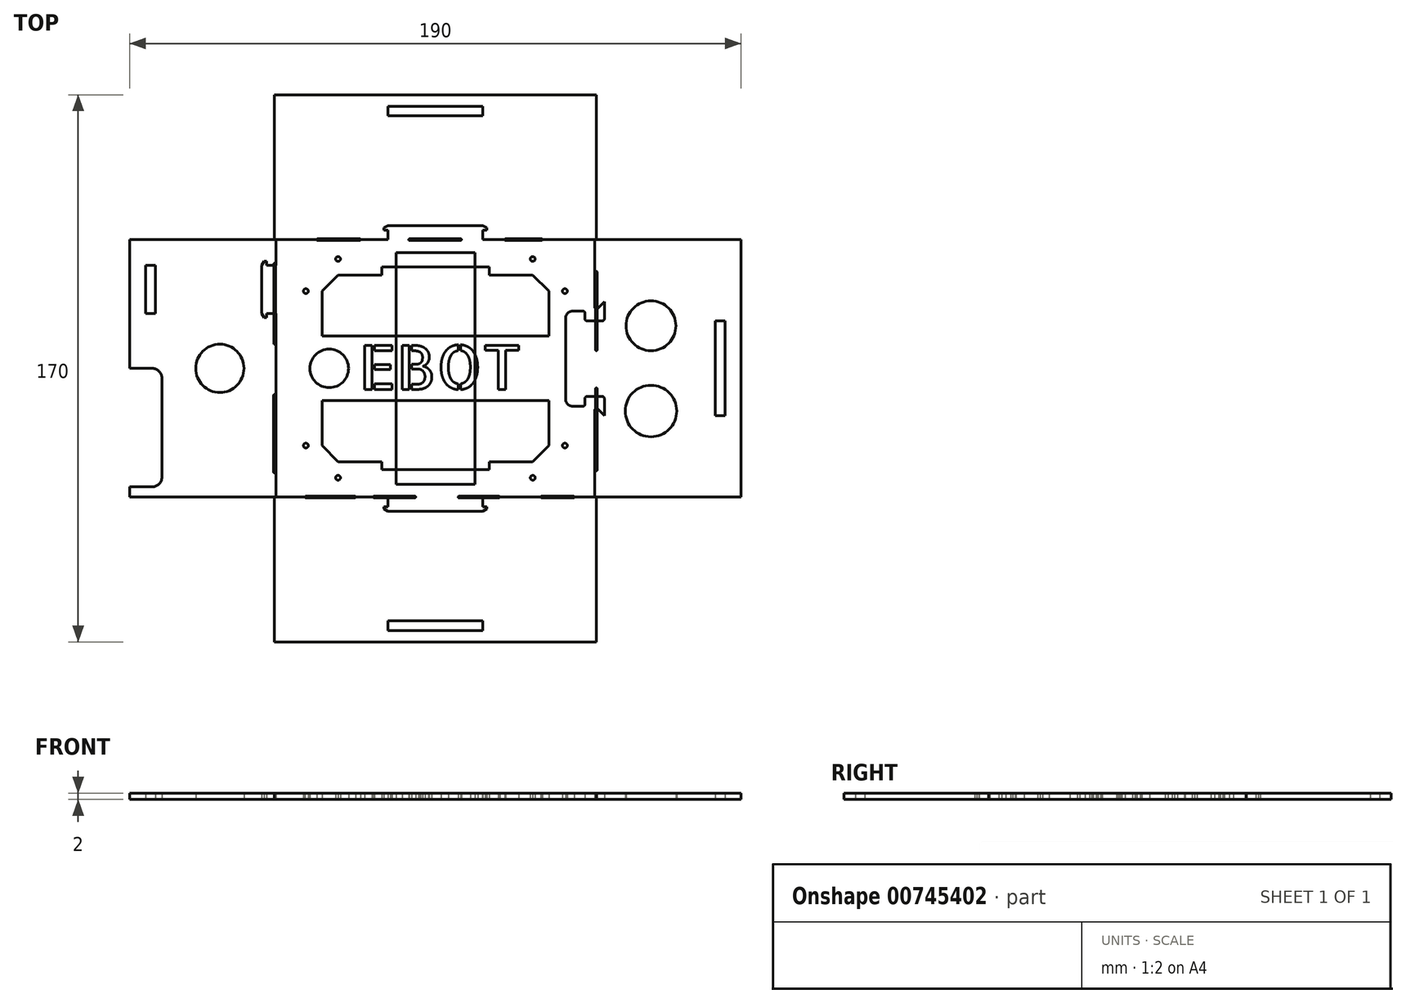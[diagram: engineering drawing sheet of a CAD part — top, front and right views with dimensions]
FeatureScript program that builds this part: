
annotation { "Feature Type Name" : "Feature", "Feature Type Description" : "" }
export const myFeature = defineFeature(function(context is Context, id is Id, definition is map)
    precondition{}
    {
        {
            var Q0;
            Q0=qCreatedBy(makeId("Top.planeOp"),FACE);
            var sketch = newSketch(context, id + "F0", { "sketchPlane" : qUnion([Q0])});
            skLineSegment(sketch, "E0.bottom", {"start": v(49.5, -40) * mm, "end": v(14.75, -40) * mm});
            skLineSegment(sketch, "E0.top", {"start": v(49.5, 40) * mm, "end": v(14.75, 40) * mm});
            skLineSegment(sketch, "E0.left", {"start": v(49.5, -40) * mm, "end": v(49.5, -13.1) * mm});
            skLineSegment(sketch, "E0.right", {"start": v(-49.5, -40) * mm, "end": v(-49.5, 17) * mm});
            skPoint(sketch, "E0.middle", {"position": v(0, 0) * mm});
            skLineSegment(sketch, "E1", {"start": v(14.75, 43) * mm, "end": v(14.75, 40) * mm});
            skLineSegment(sketch, "E2", {"start": v(-14.75, 43) * mm, "end": v(-14.75, 40) * mm});
            skLineSegment(sketch, "E3.trimOffspring", {"start": v(-14.75, 40) * mm, "end": v(-49.5, 40) * mm});
            skPoint(sketch, "E4.start.orphan", {"position": v(0, 40) * mm});
            skLineSegment(sketch, "E5", {"start": v(14.75, -43) * mm, "end": v(14.75, -40) * mm});
            skLineSegment(sketch, "E6", {"start": v(-14.75, -43) * mm, "end": v(-14.75, -40) * mm});
            skPoint(sketch, "E7.start.orphan", {"position": v(0, -40) * mm});
            skLineSegment(sketch, "E8.trimOffspring", {"start": v(-14.75, -40) * mm, "end": v(-49.5, -40) * mm});
            skLineSegment(sketch, "E9", {"start": v(-30.25, -29) * mm, "end": v(-35.25, -24) * mm});
            skLineSegment(sketch, "E10", {"start": v(30.25, -29) * mm, "end": v(35.25, -24) * mm});
            skLineSegment(sketch, "E11", {"start": v(-30.25, 29) * mm, "end": v(-35.25, 24) * mm});
            skLineSegment(sketch, "E12", {"start": v(30.25, 29) * mm, "end": v(35.25, 24) * mm});
            skLineSegment(sketch, "E13.bottom", {"start": v(35.25, -10.02) * mm, "end": v(-35.25, -10.02) * mm});
            skLineSegment(sketch, "E13.top", {"start": v(35.25, 10.02) * mm, "end": v(-35.25, 10.02) * mm});
            skLineSegment(sketch, "E14", {"start": v(-35.25, 24) * mm, "end": v(-35.25, 10.02) * mm});
            skLineSegment(sketch, "E15", {"start": v(35.25, 10.02) * mm, "end": v(35.25, 24) * mm});
            skLineSegment(sketch, "E16", {"start": v(30.25, 29) * mm, "end": v(16.69, 29) * mm});
            skLineSegment(sketch, "E17", {"start": v(35.25, -10.02) * mm, "end": v(35.25, -24) * mm});
            skLineSegment(sketch, "E18", {"start": v(30.25, -29) * mm, "end": v(16.69, -29) * mm});
            skLineSegment(sketch, "E19", {"start": v(-35.25, -24) * mm, "end": v(-35.25, -10.02) * mm});
            skLineSegment(sketch, "E20", {"start": v(35.25, 24) * mm, "end": v(40.25, 24) * mm});
            skLineSegment(sketch, "E21", {"start": v(30.25, 29) * mm, "end": v(30.25, 34) * mm});
            skLineSegment(sketch, "E22", {"start": v(-35.25, 24) * mm, "end": v(-40.25, 24) * mm});
            skLineSegment(sketch, "E23", {"start": v(-30.25, 29) * mm, "end": v(-30.25, 34) * mm});
            skLineSegment(sketch, "E24", {"start": v(-35.25, -24) * mm, "end": v(-40.25, -24) * mm});
            skLineSegment(sketch, "E25", {"start": v(-30.25, -29) * mm, "end": v(-30.25, -34) * mm});
            skLineSegment(sketch, "E26", {"start": v(35.25, -24) * mm, "end": v(40.25, -24) * mm});
            skLineSegment(sketch, "E27", {"start": v(30.25, -29) * mm, "end": v(30.25, -34) * mm});
            skLineSegment(sketch, "E28.top", {"start": v(16.69, 31.5) * mm, "end": v(-16.69, 31.5) * mm});
            skLineSegment(sketch, "E28.left", {"start": v(16.69, 29) * mm, "end": v(16.69, 31.5) * mm});
            skLineSegment(sketch, "E28.right", {"start": v(-16.69, 29) * mm, "end": v(-16.69, 31.5) * mm});
            skPoint(sketch, "E28.middle", {"position": v(0, 29) * mm});
            skLineSegment(sketch, "E29.top", {"start": v(16.69, -31.5) * mm, "end": v(-16.69, -31.5) * mm});
            skLineSegment(sketch, "E29.left", {"start": v(16.69, -29) * mm, "end": v(16.69, -31.5) * mm});
            skLineSegment(sketch, "E29.right", {"start": v(-16.69, -29) * mm, "end": v(-16.69, -31.5) * mm});
            skPoint(sketch, "E29.middle", {"position": v(0, -29) * mm});
            skLineSegment(sketch, "E30.trimOffspring", {"start": v(-16.69, 29) * mm, "end": v(-30.25, 29) * mm});
            skLineSegment(sketch, "E31.trimOffspring", {"start": v(-16.69, -29) * mm, "end": v(-30.25, -29) * mm});
            skLineSegment(sketch, "E32.bottom", {"start": v(45.49, 17.76) * mm, "end": v(42.49, 17.76) * mm});
            skLineSegment(sketch, "E32.top", {"start": v(45.49, -11.74) * mm, "end": v(42.49, -11.74) * mm});
            skLineSegment(sketch, "E32.right", {"start": v(40.49, 15.76) * mm, "end": v(40.49, -9.74) * mm});
            skPoint(sketch, "E33.visualSharp", {"position": v(40.49, 17.76) * mm});
            skArc(sketch, "E33.filletArc", {"start": v(42.49, 17.76) * mm, "mid": v(41.08, 17.17) * mm, "end": v(40.49, 15.76) * mm});
            skPoint(sketch, "E34.visualSharp", {"position": v(40.49, -11.74) * mm});
            skArc(sketch, "E34.filletArc", {"start": v(40.49, -9.74) * mm, "mid": v(41.08, -11.15) * mm, "end": v(42.49, -11.74) * mm});
            skLineSegment(sketch, "E35", {"start": v(45.49, 17.76) * mm, "end": v(45.93, 17.76) * mm});
            skLineSegment(sketch, "E36", {"start": v(45.93, -11.74) * mm, "end": v(45.49, -11.74) * mm});
            skCircle(sketch, "E37", {"center": v(30.25, 34) * mm, "radius": 0.75 * mm});
            skCircle(sketch, "E38", {"center": v(40.25, 24) * mm, "radius": 0.75 * mm});
            skCircle(sketch, "E39", {"center": v(40.25, -24) * mm, "radius": 0.75 * mm});
            skCircle(sketch, "E40", {"center": v(30.25, -34) * mm, "radius": 0.75 * mm});
            skCircle(sketch, "E41", {"center": v(-30.25, -34) * mm, "radius": 0.75 * mm});
            skCircle(sketch, "E42", {"center": v(-40.25, -24) * mm, "radius": 0.75 * mm});
            skCircle(sketch, "E43", {"center": v(-40.25, 24) * mm, "radius": 0.75 * mm});
            skCircle(sketch, "E44", {"center": v(-30.25, 34) * mm, "radius": 0.75 * mm});
            skLineSegment(sketch, "E45.bottom", {"start": v(14.75, 44.4) * mm, "end": v(-14.75, 44.4) * mm});
            skLineSegment(sketch, "E45.left", {"start": v(16, 43.7) * mm, "end": v(16, 43) * mm});
            skLineSegment(sketch, "E45.right", {"start": v(-16, 43.7) * mm, "end": v(-16, 43) * mm});
            skPoint(sketch, "E45.middle", {"position": v(0, 43) * mm});
            skLineSegment(sketch, "E46", {"start": v(-16, 43) * mm, "end": v(-14.75, 43) * mm});
            skPoint(sketch, "E47.orphan", {"position": v(16, 41.6) * mm});
            skPoint(sketch, "E48.orphan", {"position": v(-16, 41.6) * mm});
            skLineSegment(sketch, "E49.trimOffspring", {"start": v(14.75, 43) * mm, "end": v(16, 43) * mm});
            skLineSegment(sketch, "E50", {"start": v(16, 43.7) * mm, "end": v(14.75, 44.4) * mm});
            skLineSegment(sketch, "E51", {"start": v(-16, 43.7) * mm, "end": v(-14.75, 44.4) * mm});
            skPoint(sketch, "E52.orphan", {"position": v(-16, 44.4) * mm});
            skPoint(sketch, "E53.orphan", {"position": v(16, 44.4) * mm});
            skLineSegment(sketch, "E54.MirrorCS", {"start": v(16, -43.7) * mm, "end": v(16, -43) * mm});
            skLineSegment(sketch, "E55.MirrorCS", {"start": v(-16, -43.7) * mm, "end": v(-16, -43) * mm});
            skLineSegment(sketch, "E56.MirrorCS", {"start": v(-16, -43.7) * mm, "end": v(-14.75, -44.4) * mm});
            skLineSegment(sketch, "E57.MirrorCS", {"start": v(14.75, -43) * mm, "end": v(16, -43) * mm});
            skLineSegment(sketch, "E58.MirrorCS", {"start": v(16, -43.7) * mm, "end": v(14.75, -44.4) * mm});
            skLineSegment(sketch, "E59.MirrorCS", {"start": v(-16, -43) * mm, "end": v(-14.75, -43) * mm});
            skLineSegment(sketch, "E60.MirrorCS", {"start": v(14.75, -44.4) * mm, "end": v(-14.75, -44.4) * mm});
            skPoint(sketch, "E61.MirrorP", {"position": v(0, -43) * mm});
            skPoint(sketch, "E62.MirrorP", {"position": v(16, -41.6) * mm});
            skPoint(sketch, "E63.MirrorP", {"position": v(16, -44.4) * mm});
            skPoint(sketch, "E64.MirrorP", {"position": v(-16, -41.6) * mm});
            skPoint(sketch, "E65.MirrorP", {"position": v(-16, -44.4) * mm});
            skLineSegment(sketch, "E66", {"start": v(-49.5, 40) * mm, "end": v(-49.5, 32) * mm, "construction": true});
            skLineSegment(sketch, "E67", {"start": v(-49.5, 32) * mm, "end": v(-52.5, 32) * mm});
            skLineSegment(sketch, "E68", {"start": v(-52.5, 17) * mm, "end": v(-49.5, 17) * mm});
            skLineSegment(sketch, "E69.bottom", {"start": v(-52.5, 15.75) * mm, "end": v(-53.25, 15.75) * mm});
            skLineSegment(sketch, "E69.top", {"start": v(-52.5, 33.25) * mm, "end": v(-53.25, 33.25) * mm});
            skLineSegment(sketch, "E69.right", {"start": v(-54, 17) * mm, "end": v(-54, 32) * mm});
            skPoint(sketch, "E69.cornerSnap0", {"position": v(-51, 17) * mm});
            skLineSegment(sketch, "E70", {"start": v(-52.5, 33.25) * mm, "end": v(-52.5, 32) * mm});
            skPoint(sketch, "E71.orphan", {"position": v(-51, 15.75) * mm});
            skPoint(sketch, "E72.orphan", {"position": v(-51, 33.25) * mm});
            skLineSegment(sketch, "E73", {"start": v(-53.25, 33.25) * mm, "end": v(-54, 32) * mm});
            skLineSegment(sketch, "E74", {"start": v(-53.25, 15.75) * mm, "end": v(-54, 17) * mm});
            skPoint(sketch, "E75.orphan", {"position": v(-54, 15.75) * mm});
            skPoint(sketch, "E76.orphan", {"position": v(-54, 33.25) * mm});
            skLineSegment(sketch, "E77.trimOffspring", {"start": v(-52.5, 17) * mm, "end": v(-52.5, 15.75) * mm});
            skLineSegment(sketch, "E78.trimOffspring", {"start": v(-49.5, 32) * mm, "end": v(-49.5, 40) * mm});
            skLineSegment(sketch, "E79", {"start": v(49.5, 40) * mm, "end": v(49.5, 19.13) * mm});
            skLineSegment(sketch, "E80.bottom", {"start": v(51.93, 14.76) * mm, "end": v(47.07, 14.76) * mm});
            skLineSegment(sketch, "E80.left", {"start": v(52.5, 15.33) * mm, "end": v(52.5, 20.76) * mm});
            skLineSegment(sketch, "E80.right", {"start": v(46.5, 15.33) * mm, "end": v(46.5, 17.2) * mm});
            skPoint(sketch, "E80.middle", {"position": v(49.5, 17.76) * mm});
            skLineSegment(sketch, "E81.top", {"start": v(51.93, -8.74) * mm, "end": v(47.07, -8.74) * mm});
            skLineSegment(sketch, "E81.left", {"start": v(52.5, -14.74) * mm, "end": v(52.5, -9.3) * mm});
            skPoint(sketch, "E81.middle", {"position": v(49.5, -11.74) * mm});
            skLineSegment(sketch, "E82", {"start": v(50.47, 18.73) * mm, "end": v(52.5, 20.76) * mm});
            skLineSegment(sketch, "E83", {"start": v(50.47, -12.7) * mm, "end": v(52.5, -14.74) * mm});
            skLineSegment(sketch, "E84", {"start": v(46.5, -9.3) * mm, "end": v(46.5, -11.17) * mm});
            skArc(sketch, "E85.filletArc", {"start": v(45.93, -11.74) * mm, "mid": v(46.33, -11.57) * mm, "end": v(46.5, -11.17) * mm});
            skPoint(sketch, "E86.visualSharp", {"position": v(46.5, -8.74) * mm});
            skArc(sketch, "E86.filletArc", {"start": v(47.07, -8.74) * mm, "mid": v(46.67, -8.9) * mm, "end": v(46.5, -9.3) * mm});
            skPoint(sketch, "E87.visualSharp", {"position": v(52.5, -8.74) * mm});
            skArc(sketch, "E87.filletArc", {"start": v(52.5, -9.3) * mm, "mid": v(52.33, -8.9) * mm, "end": v(51.93, -8.74) * mm});
            skArc(sketch, "E88.filletArc", {"start": v(50.47, -12.7) * mm, "mid": v(49.85, -12.58) * mm, "end": v(49.5, -13.1) * mm});
            skPoint(sketch, "E80.top.end.orphan", {"position": v(46.5, 20.76) * mm});
            skPoint(sketch, "E89.visualSharp", {"position": v(46.5, 17.76) * mm});
            skArc(sketch, "E89.filletArc", {"start": v(46.5, 17.2) * mm, "mid": v(46.33, 17.6) * mm, "end": v(45.93, 17.76) * mm});
            skPoint(sketch, "E90.visualSharp", {"position": v(46.5, 14.76) * mm});
            skArc(sketch, "E90.filletArc", {"start": v(46.5, 15.33) * mm, "mid": v(46.67, 14.93) * mm, "end": v(47.07, 14.76) * mm});
            skPoint(sketch, "E91.visualSharp", {"position": v(52.5, 14.76) * mm});
            skArc(sketch, "E91.filletArc", {"start": v(51.93, 14.76) * mm, "mid": v(52.33, 14.93) * mm, "end": v(52.5, 15.33) * mm});
            skArc(sketch, "E92.filletArc", {"start": v(49.5, 19.13) * mm, "mid": v(49.85, 18.6) * mm, "end": v(50.47, 18.73) * mm});
            skText(sketch, "E93", { "text": "EBOT", "fontName": "AllertaStencil-Regular.ttf"});
            skLineSegment(sketch, "E94", {"start": v(-35.25, 24) * mm, "end": v(-35.25, 29) * mm, "construction": true});
            skLineSegment(sketch, "E95", {"start": v(-35.25, 29) * mm, "end": v(-30.25, 29) * mm, "construction": true});
            skLineSegment(sketch, "E96", {"start": v(30.25, 29) * mm, "end": v(35.25, 29) * mm, "construction": true});
            skLineSegment(sketch, "E97", {"start": v(35.25, 29) * mm, "end": v(35.25, 24) * mm, "construction": true});
            skLineSegment(sketch, "E98", {"start": v(35.25, -24) * mm, "end": v(35.25, -29) * mm, "construction": true});
            skLineSegment(sketch, "E99", {"start": v(35.25, -29) * mm, "end": v(30.25, -29) * mm, "construction": true});
            skLineSegment(sketch, "E100", {"start": v(-35.25, -24) * mm, "end": v(-35.25, -29) * mm, "construction": true});
            skLineSegment(sketch, "E101", {"start": v(-35.25, -29) * mm, "end": v(-30.25, -29) * mm, "construction": true});
            const initialGuessF0  = {"E93": [-0.02376, -0.00652, 1, 0, 0.01367]};
            skSetInitialGuess(sketch, initialGuessF0);
            skSolve(sketch);
        }
        {
            var Q0;
            Q0=qCreatedBy(makeId("Top.planeOp"),FACE);
            var sketch = newSketch(context, id + "F1", { "sketchPlane" : qUnion([Q0])});
            skLineSegment(sketch, "E102.bottom", {"start": v(50, -40) * mm, "end": v(50, -85) * mm});
            skLineSegment(sketch, "E103.top", {"start": v(95, -40) * mm, "end": v(95, 40) * mm});
            skLineSegment(sketch, "E103.left", {"start": v(50, -40) * mm, "end": v(72.5, -40) * mm});
            skLineSegment(sketch, "E103.right", {"start": v(50, 40) * mm, "end": v(72.5, 40) * mm});
            skLineSegment(sketch, "E104.bottom", {"start": v(50, 40) * mm, "end": v(50, 85) * mm});
            skLineSegment(sketch, "E104.top", {"start": v(-50, 40) * mm, "end": v(-50, 85) * mm});
            skLineSegment(sketch, "E104.right", {"start": v(50, 85) * mm, "end": v(-50, 85) * mm});
            skLineSegment(sketch, "E105.top", {"start": v(-95, 40) * mm, "end": v(-95, 0) * mm});
            skLineSegment(sketch, "E105.left", {"start": v(-49.99, 40) * mm, "end": v(-72.5, 40) * mm});
            skLineSegment(sketch, "E105.right", {"start": v(-50, -40) * mm, "end": v(-72.5, -40) * mm});
            skLineSegment(sketch, "E106", {"start": v(-50, 0) * mm, "end": v(-67, 0) * mm, "construction": true});
            skPoint(sketch, "E107.startSnap0", {"position": v(0, -40) * mm});
            skLineSegment(sketch, "E108", {"start": v(-50, -85) * mm, "end": v(50, -85) * mm});
            skLineSegment(sketch, "E109", {"start": v(-50, -85) * mm, "end": v(-50, -40) * mm});
            skLineSegment(sketch, "E110", {"start": v(0, -85) * mm, "end": v(0, -80) * mm, "construction": true});
            skLineSegment(sketch, "E111.bottom", {"start": v(14.75, -81.5) * mm, "end": v(-14.75, -81.5) * mm});
            skLineSegment(sketch, "E111.top", {"start": v(14.75, -78.5) * mm, "end": v(-14.75, -78.5) * mm});
            skLineSegment(sketch, "E111.left", {"start": v(14.75, -81.5) * mm, "end": v(14.75, -78.5) * mm});
            skLineSegment(sketch, "E111.right", {"start": v(-14.75, -81.5) * mm, "end": v(-14.75, -78.5) * mm});
            skPoint(sketch, "E111.middle", {"position": v(0, -80) * mm});
            skLineSegment(sketch, "E112", {"start": v(0, 85) * mm, "end": v(0, 80) * mm, "construction": true});
            skLineSegment(sketch, "E113.bottom", {"start": v(14.75, 78.5) * mm, "end": v(-14.75, 78.5) * mm});
            skLineSegment(sketch, "E113.top", {"start": v(14.75, 81.5) * mm, "end": v(-14.75, 81.5) * mm});
            skLineSegment(sketch, "E113.left", {"start": v(14.75, 78.5) * mm, "end": v(14.75, 81.5) * mm});
            skLineSegment(sketch, "E113.right", {"start": v(-14.75, 78.5) * mm, "end": v(-14.75, 81.5) * mm});
            skPoint(sketch, "E113.middle", {"position": v(0, 80) * mm});
            skLineSegment(sketch, "E114", {"start": v(-95, 0) * mm, "end": v(-85, 0) * mm, "construction": true});
            skLineSegment(sketch, "E115", {"start": v(-95, 0) * mm, "end": v(-88, 0) * mm});
            skLineSegment(sketch, "E116", {"start": v(-85, -33.83) * mm, "end": v(-85, -3) * mm});
            skPoint(sketch, "E117.visualSharp", {"position": v(-85, 0) * mm});
            skArc(sketch, "E117.filletArc", {"start": v(-85, -3) * mm, "mid": v(-85.88, -0.88) * mm, "end": v(-88, 0) * mm});
            skLineSegment(sketch, "E118", {"start": v(-88, -36.83) * mm, "end": v(-95, -36.83) * mm});
            skArc(sketch, "E119.filletArc", {"start": v(-88, -36.83) * mm, "mid": v(-85.88, -35.95) * mm, "end": v(-85, -33.83) * mm});
            skLineSegment(sketch, "E120.trimOffspring", {"start": v(-95, -36.83) * mm, "end": v(-95, -40) * mm});
            skCircle(sketch, "E121", {"center": v(-33, 0) * mm, "radius": 6 * mm});
            skCircle(sketch, "E122", {"center": v(-67, 0) * mm, "radius": 7.5 * mm});
            skLineSegment(sketch, "E123", {"start": v(50, 40) * mm, "end": v(33, 40) * mm, "construction": true});
            skLineSegment(sketch, "E124", {"start": v(50, 0) * mm, "end": v(67, 0) * mm, "construction": true});
            skLineSegment(sketch, "E125.trimOffspring", {"start": v(87.5, 40) * mm, "end": v(95, 40) * mm});
            skPoint(sketch, "E126.oppositeSnap0", {"position": v(72.5, -40) * mm});
            skLineSegment(sketch, "E127.trimOffspring", {"start": v(87.5, -40) * mm, "end": v(95, -40) * mm});
            skPoint(sketch, "E128.firstSnap0", {"position": v(-72.5, -40) * mm});
            skLineSegment(sketch, "E128.bottom", {"start": v(-72.5, -40) * mm, "end": v(-72.5, -40) * mm});
            skLineSegment(sketch, "E129.trimOffspring", {"start": v(-87.5, -40) * mm, "end": v(-95, -40) * mm});
            skLineSegment(sketch, "E130.trimOffspring", {"start": v(-87.5, 40) * mm, "end": v(-95, 40) * mm});
            skLineSegment(sketch, "E131", {"start": v(-87.5, 40) * mm, "end": v(-72.5, 40) * mm});
            skLineSegment(sketch, "E132", {"start": v(-72.5, -40) * mm, "end": v(-87.5, -40) * mm});
            skLineSegment(sketch, "E133", {"start": v(72.5, -40) * mm, "end": v(87.5, -40) * mm});
            skLineSegment(sketch, "E134", {"start": v(-49.99, 32.47) * mm, "end": v(-49.99, 7.79) * mm});
            skLineSegment(sketch, "E135", {"start": v(-50, -32.3) * mm, "end": v(-50, -8.35) * mm});
            skLineSegment(sketch, "E136", {"start": v(50, 29.94) * mm, "end": v(50, 5.74) * mm});
            skLineSegment(sketch, "E137", {"start": v(50, -31.59) * mm, "end": v(50, -6.35) * mm});
            skLineSegment(sketch, "E138", {"start": v(-40.23, -40) * mm, "end": v(-25.04, -40) * mm});
            skLineSegment(sketch, "E139", {"start": v(72.5, 40) * mm, "end": v(87.5, 40) * mm});
            skLineSegment(sketch, "E140.bottom", {"start": v(12.25, -36) * mm, "end": v(-12.25, -36) * mm});
            skLineSegment(sketch, "E140.top", {"start": v(12.25, 36) * mm, "end": v(-12.25, 36) * mm});
            skLineSegment(sketch, "E140.left", {"start": v(12.25, -36) * mm, "end": v(12.25, 36) * mm});
            skLineSegment(sketch, "E140.right", {"start": v(-12.25, -36) * mm, "end": v(-12.25, 36) * mm});
            skPoint(sketch, "E140.middle", {"position": v(0, 0) * mm});
            skLineSegment(sketch, "E141", {"start": v(67, 0) * mm, "end": v(67, 5.5) * mm, "construction": true});
            skLineSegment(sketch, "E142", {"start": v(67, 0) * mm, "end": v(67, -5.25) * mm, "construction": true});
            skLineSegment(sketch, "E143", {"start": v(67, -5.25) * mm, "end": v(67, -13.25) * mm, "construction": true});
            skCircle(sketch, "E144", {"center": v(67, -13.25) * mm, "radius": 8 * mm});
            skLineSegment(sketch, "E145", {"start": v(67, 5.25) * mm, "end": v(67, 13.25) * mm, "construction": true});
            skCircle(sketch, "E146", {"center": v(67, 13.25) * mm, "radius": 7.75 * mm});
            skLineSegment(sketch, "E147.3.0", {"start": v(87, -14.75) * mm, "end": v(90, -14.75) * mm});
            skLineSegment(sketch, "E147.3.1", {"start": v(87, -14.75) * mm, "end": v(87, 14.75) * mm});
            skLineSegment(sketch, "E147.3.2", {"start": v(90, -14.75) * mm, "end": v(90, 14.75) * mm});
            skLineSegment(sketch, "E147.3.3", {"start": v(87, 14.75) * mm, "end": v(90, 14.75) * mm});
            skPoint(sketch, "E147.center", {"position": v(4.25, -4.25) * mm});
            skLineSegment(sketch, "E148.bottom", {"start": v(-90, 32) * mm, "end": v(-87, 32) * mm});
            skLineSegment(sketch, "E148.top", {"start": v(-90, 17) * mm, "end": v(-87, 17) * mm});
            skLineSegment(sketch, "E148.left", {"start": v(-90, 32) * mm, "end": v(-90, 17) * mm});
            skLineSegment(sketch, "E148.right", {"start": v(-87, 32) * mm, "end": v(-87, 17) * mm});
            skLineSegment(sketch, "E149", {"start": v(-19.03, -39.98) * mm, "end": v(-6.4, -39.98) * mm});
            skLineSegment(sketch, "E150", {"start": v(-6.4, -39.98) * mm, "end": v(7.31, -39.98) * mm, "construction": true});
            skLineSegment(sketch, "E151", {"start": v(7.31, -39.98) * mm, "end": v(19.74, -40) * mm});
            skLineSegment(sketch, "E152", {"start": v(19.74, -40) * mm, "end": v(33, -40) * mm, "construction": true});
            skLineSegment(sketch, "E153", {"start": v(33, -40) * mm, "end": v(42.95, -40) * mm});
            skLineSegment(sketch, "E154", {"start": v(42.95, -40) * mm, "end": v(50, -40) * mm, "construction": true});
            skLineSegment(sketch, "E155", {"start": v(-49.99, 40) * mm, "end": v(-36.6, 40) * mm, "construction": true});
            skLineSegment(sketch, "E156", {"start": v(-36.6, 40) * mm, "end": v(-23.54, 40) * mm});
            skLineSegment(sketch, "E157", {"start": v(-23.54, 40) * mm, "end": v(-8.07, 40) * mm, "construction": true});
            skLineSegment(sketch, "E158", {"start": v(-8.07, 40) * mm, "end": v(7.85, 40) * mm});
            skLineSegment(sketch, "E159", {"start": v(7.85, 40) * mm, "end": v(21.78, 40) * mm, "construction": true});
            skLineSegment(sketch, "E160", {"start": v(21.78, 40) * mm, "end": v(33, 40) * mm});
            skArc(sketch, "E161.0.startCap", {"start": v(49.75, 29.94) * mm, "mid": v(50, 30.2) * mm, "end": v(50.25, 29.94) * mm});
            skArc(sketch, "E161.0.endCap", {"start": v(50.25, 5.74) * mm, "mid": v(50, 5.5) * mm, "end": v(49.75, 5.74) * mm});
            skLineSegment(sketch, "E161.0.left", {"start": v(50.25, 29.94) * mm, "end": v(50.25, 5.74) * mm});
            skLineSegment(sketch, "E161.0.right", {"start": v(49.75, 29.94) * mm, "end": v(49.75, 5.74) * mm});
            skArc(sketch, "E162.0.startCap", {"start": v(50.25, -31.59) * mm, "mid": v(50, -31.84) * mm, "end": v(49.75, -31.59) * mm});
            skArc(sketch, "E162.0.endCap", {"start": v(49.75, -6.35) * mm, "mid": v(50, -6.1) * mm, "end": v(50.25, -6.35) * mm});
            skLineSegment(sketch, "E162.0.left", {"start": v(49.75, -31.59) * mm, "end": v(49.75, -6.35) * mm});
            skLineSegment(sketch, "E162.0.right", {"start": v(50.25, -31.59) * mm, "end": v(50.25, -6.35) * mm});
            skArc(sketch, "E162.1.startCap", {"start": v(33, -40.25) * mm, "mid": v(32.74, -40) * mm, "end": v(33, -39.75) * mm});
            skArc(sketch, "E162.1.endCap", {"start": v(42.95, -39.75) * mm, "mid": v(43.2, -40) * mm, "end": v(42.95, -40.25) * mm});
            skLineSegment(sketch, "E162.1.left", {"start": v(33, -39.75) * mm, "end": v(42.95, -39.75) * mm});
            skLineSegment(sketch, "E162.1.right", {"start": v(33, -40.25) * mm, "end": v(42.95, -40.25) * mm});
            skArc(sketch, "E162.2.startCap", {"start": v(7.31, -40.23) * mm, "mid": v(7.06, -39.98) * mm, "end": v(7.31, -39.73) * mm});
            skArc(sketch, "E162.2.endCap", {"start": v(19.74, -39.75) * mm, "mid": v(20, -40) * mm, "end": v(19.74, -40.25) * mm});
            skLineSegment(sketch, "E162.2.left", {"start": v(7.31, -39.73) * mm, "end": v(19.74, -39.75) * mm});
            skLineSegment(sketch, "E162.2.right", {"start": v(7.31, -40.23) * mm, "end": v(19.74, -40.25) * mm});
            skArc(sketch, "E162.3.startCap", {"start": v(-19.03, -40.23) * mm, "mid": v(-19.28, -39.98) * mm, "end": v(-19.03, -39.73) * mm});
            skArc(sketch, "E162.3.endCap", {"start": v(-6.4, -39.73) * mm, "mid": v(-6.16, -39.98) * mm, "end": v(-6.4, -40.23) * mm});
            skLineSegment(sketch, "E162.3.left", {"start": v(-19.03, -39.73) * mm, "end": v(-6.4, -39.73) * mm});
            skLineSegment(sketch, "E162.3.right", {"start": v(-19.03, -40.23) * mm, "end": v(-6.4, -40.23) * mm});
            skArc(sketch, "E162.4.startCap", {"start": v(-40.23, -40.25) * mm, "mid": v(-40.48, -40) * mm, "end": v(-40.23, -39.75) * mm});
            skArc(sketch, "E162.4.endCap", {"start": v(-25.04, -39.75) * mm, "mid": v(-24.79, -40) * mm, "end": v(-25.04, -40.25) * mm});
            skLineSegment(sketch, "E162.4.left", {"start": v(-40.23, -39.75) * mm, "end": v(-25.04, -39.75) * mm});
            skLineSegment(sketch, "E162.4.right", {"start": v(-40.23, -40.25) * mm, "end": v(-25.04, -40.25) * mm});
            skArc(sketch, "E162.5.startCap", {"start": v(-49.75, -32.3) * mm, "mid": v(-50, -32.55) * mm, "end": v(-50.25, -32.3) * mm});
            skArc(sketch, "E162.5.endCap", {"start": v(-50.25, -8.35) * mm, "mid": v(-50, -8.1) * mm, "end": v(-49.75, -8.35) * mm});
            skLineSegment(sketch, "E162.5.left", {"start": v(-50.25, -32.3) * mm, "end": v(-50.25, -8.35) * mm});
            skLineSegment(sketch, "E162.5.right", {"start": v(-49.75, -32.3) * mm, "end": v(-49.75, -8.35) * mm});
            skArc(sketch, "E162.6.startCap", {"start": v(21.78, 39.75) * mm, "mid": v(21.53, 40) * mm, "end": v(21.78, 40.25) * mm});
            skArc(sketch, "E162.6.endCap", {"start": v(33, 40.25) * mm, "mid": v(33.25, 40) * mm, "end": v(33, 39.75) * mm});
            skLineSegment(sketch, "E162.6.left", {"start": v(21.78, 40.25) * mm, "end": v(33, 40.25) * mm});
            skLineSegment(sketch, "E162.6.right", {"start": v(21.78, 39.75) * mm, "end": v(33, 39.75) * mm});
            skArc(sketch, "E162.7.startCap", {"start": v(-8.07, 39.75) * mm, "mid": v(-8.32, 40) * mm, "end": v(-8.07, 40.25) * mm});
            skArc(sketch, "E162.7.endCap", {"start": v(7.85, 40.25) * mm, "mid": v(8.1, 40) * mm, "end": v(7.85, 39.75) * mm});
            skLineSegment(sketch, "E162.7.left", {"start": v(-8.07, 40.25) * mm, "end": v(7.85, 40.25) * mm});
            skLineSegment(sketch, "E162.7.right", {"start": v(-8.07, 39.75) * mm, "end": v(7.85, 39.75) * mm});
            skArc(sketch, "E162.8.startCap", {"start": v(-36.6, 39.75) * mm, "mid": v(-36.85, 40) * mm, "end": v(-36.6, 40.25) * mm});
            skArc(sketch, "E162.8.endCap", {"start": v(-23.54, 40.25) * mm, "mid": v(-23.3, 40) * mm, "end": v(-23.54, 39.75) * mm});
            skLineSegment(sketch, "E162.8.left", {"start": v(-36.6, 40.25) * mm, "end": v(-23.54, 40.25) * mm});
            skLineSegment(sketch, "E162.8.right", {"start": v(-36.6, 39.75) * mm, "end": v(-23.54, 39.75) * mm});
            skArc(sketch, "E162.9.startCap", {"start": v(-50.24, 32.47) * mm, "mid": v(-49.99, 32.72) * mm, "end": v(-49.74, 32.47) * mm});
            skArc(sketch, "E162.9.endCap", {"start": v(-49.74, 7.79) * mm, "mid": v(-49.99, 7.54) * mm, "end": v(-50.24, 7.79) * mm});
            skLineSegment(sketch, "E162.9.left", {"start": v(-49.74, 32.47) * mm, "end": v(-49.74, 7.79) * mm});
            skLineSegment(sketch, "E162.9.right", {"start": v(-50.24, 32.47) * mm, "end": v(-50.24, 7.79) * mm});
            skSolve(sketch);
        }
        {
            var Q0;
            Q0=makeQuery(id+"F1.imprint","IMPRINT",FACE,{"disambiguationData":[TD([[makeQuery(id+"F1.imprint","IMPRINT",EDGE,{"derivedFrom":sQuery(id+"F1.wireOp",EDGE,"E102.bottom")}),-1.0]])]});
            extrude(context, id + "F2", {"entities" : qUnion([Q0]), "depth" : 2 * mm, "offsetDistance" : 25 * mm});
        }
        {
            var Q0;
            Q0=makeQuery(id+"F0.imprint","IMPRINT",FACE,{"disambiguationData":[TD([[makeQuery(id+"F0.imprint","IMPRINT",EDGE,{"derivedFrom":sQuery(id+"F0.wireOp",EDGE,"E0.bottom")}),-1.0]])]});
            extrude(context, id + "F3", {"entities" : qUnion([Q0]), "depth" : 2 * mm, "offsetDistance" : 25 * mm});
        }
    });
